FREECAD ASSEMBLY — COMPONENT RECIPES ("assambly-control-assembly")

This assembly document has 2 components, labeled P0..P1 below (a component is one placed body or linked part). 2 of them carry a construction recipe — the FreeCAD feature program that regenerates the part from scratch, quoted from this document or its linked companion documents; the rest are supplied as boundary geometry only. No exploded tour is included for this assembly.
COMPONENT P0 — recipe-attached ("SideBody", a linked part whose construction recipe lives in a companion FreeCAD document of the same project; that document's serialized recipe follows).
Construction recipe (the companion document, serialized — sketch geometry with constraints, then the solid features built on it; lengths are millimeters unless a unit is written):

FCSTD DOCUMENT  (FreeCAD 1.0RUnknown)
Label: assambly-control-varset
License: All rights reserved
LicenseURL: https://en.wikipedia.org/wiki/All_rights_reserved
objects: Sketcher::SketchObject×3, PartDesign::Pad×2, PartDesign::Body×2, App::VarSet×1
note: 14 computed .brp shape members not serialized (recipe doc carries the construction recipe); baked Part::Feature solids carry a one-line shape summary decoded from their .brp

FEATURE [Sketcher::SketchObject] Sketch  label="SkeletonSketch"
  ArcFitTolerance = 1e-06
  FullyConstrained = true
  MakeInternals = false
  Placement = pos=(0,0,0) rot=(1,0,0;1.5708rad)
  expr: Constraints[20] = VarSet.Shelf3Haight
  expr: Constraints[21] = VarSet.Shelf2Height
  expr: Constraints[22] = VarSet.Shelf1Height
  expr: Constraints[7] = VarSet.CabWidth
  expr: Constraints[8] = VarSet.CabHeight
  sketch-geometry (7):
    g0: LineSegment StartX=-500 StartY=0 StartZ=0 EndX=500 EndY=0 EndZ=0
    g1: LineSegment StartX=500 StartY=0 StartZ=0 EndX=500 EndY=2500 EndZ=0
    g2: LineSegment StartX=500 StartY=2500 StartZ=0 EndX=-500 EndY=2500 EndZ=0
    g3: LineSegment StartX=-500 StartY=2500 StartZ=0 EndX=-500 EndY=0 EndZ=0
    g4: LineSegment StartX=-500 StartY=500 StartZ=0 EndX=500 EndY=500 EndZ=0
    g5: LineSegment StartX=-500 StartY=1000 StartZ=0 EndX=500 EndY=1000 EndZ=0
    g6: LineSegment StartX=-500 StartY=1500 StartZ=0 EndX=500 EndY=1500 EndZ=0
  constraints (23):
    c: Coincident(g0,g1)
    c: Coincident(g1,g2)
    c: Coincident(g2,g3)
    c: Coincident(g3,g0)
    c: Horizontal(g2)
    c: Vertical(g1)
    c: Vertical(g3)
    c: Distance(g1,g3) = 1000
    c: Distance(g0,g2) = 2500
    c: PointOnObject(g0,g-1)
    c: Symmetric(g0,g0,g-2)
    c: PointOnObject(g4,g3)
    c: PointOnObject(g4,g1)
    c: Horizontal(g4)
    c: PointOnObject(g5,g3)
    c: PointOnObject(g5,g1)
    c: Horizontal(g5)
    c: PointOnObject(g6,g3)
    c: PointOnObject(g6,g1)
    c: Horizontal(g6)
    c: DistanceY(g-1,g4) = 500
    c: DistanceY(g-1,g5) = 1000
    c: DistanceY(g-1,g6) = 1500
FEATURE [App::VarSet] VarSet
  CabHeight = 2580
  CabWidth = 1000
  Shelf1Height = 1500
  Shelf2Height = 1000
  Shelf3Haight = 500
FEATURE [Sketcher::SketchObject] Sketch001
  ArcFitTolerance = 1e-06
  AttachmentSupport = -> [YZ_Plane]
  FullyConstrained = true
  MakeInternals = false
  MapMode = 5
  Placement = pos=(0,0,0) rot=(0.57735,0.57735,0.57735;2.0944rad)
  expr: Constraints[8] = VarSet.CabWidth
  expr: Constraints[9] = VarSet.CabHeight
  sketch-geometry (4):
    g0: LineSegment StartX=-500 StartY=0 StartZ=0 EndX=500 EndY=0 EndZ=0
    g1: LineSegment StartX=500 StartY=0 StartZ=0 EndX=500 EndY=2500 EndZ=0
    g2: LineSegment StartX=500 StartY=2500 StartZ=0 EndX=-500 EndY=2500 EndZ=0
    g3: LineSegment StartX=-500 StartY=2500 StartZ=0 EndX=-500 EndY=0 EndZ=0
  constraints (11):
    c: Coincident(g0,g1)
    c: Coincident(g1,g2)
    c: Coincident(g2,g3)
    c: Coincident(g3,g0)
    c: Horizontal(g0)
    c: Horizontal(g2)
    c: Vertical(g1)
    c: Vertical(g3)
    c: Distance(g0,g0) = 1000
    c: DistanceY(g1,g1) = 2500
    c: Symmetric(g0,g0,g-1)
FEATURE [PartDesign::Pad] Pad
  Direction = (1,0,0)
  Length = 30
  Length2 = 10
  Placement = pos=(0,0,0) rot=(1,1,1;2.0944rad)
  Profile = -> Sketch001
  ReferenceAxis = -> Sketch001 [N_Axis]
  Refine = true
  Suppressed = false
  Type = 0
FEATURE [PartDesign::Body] Body  label="SideBody"
  AllowCompound = false
  Group = -> [Sketch001,Pad]
  Origin = -> Origin
  Tip = -> Pad
FEATURE [Sketcher::SketchObject] Sketch002
  ArcFitTolerance = 1e-06
  AttachmentSupport = -> [XY_Plane001]
  FullyConstrained = true
  MakeInternals = false
  MapMode = 5
  expr: Constraints[10] = VarSet.CabWidth
  sketch-geometry (5):
    g0: LineSegment StartX=500 StartY=-500 StartZ=0 EndX=500 EndY=500 EndZ=0
    g1: LineSegment StartX=500 StartY=500 StartZ=0 EndX=-500 EndY=500 EndZ=0
    g2: LineSegment StartX=-500 StartY=500 StartZ=0 EndX=-500 EndY=-500 EndZ=0
    g3: LineSegment StartX=-500 StartY=-500 StartZ=0 EndX=500 EndY=-500 EndZ=0
    g4: GeomPoint [constr] X=0 Y=0 Z=0
  constraints (12):
    c: Coincident(g0,g1)
    c: Coincident(g1,g2)
    c: Coincident(g2,g3)
    c: Coincident(g3,g0)
    c: Vertical(g0)
    c: Vertical(g2)
    c: Horizontal(g1)
    c: Horizontal(g3)
    c: Symmetric(g2,g0,g4)
    c: Coincident(g4,g-1)
    c: DistanceY(g2,g2) = 1000
    c: Equal(g2,g1)
FEATURE [PartDesign::Pad] Pad001
  Direction = (0,0,1)
  Length = 30
  Length2 = 10
  Profile = -> Sketch002
  ReferenceAxis = -> Sketch002 [N_Axis]
  Refine = true
  Suppressed = false
  Type = 0
FEATURE [PartDesign::Body] Body001  label="ShelfBody"
  AllowCompound = false
  Group = -> [Sketch002,Pad001]
  Origin = -> Origin001
  Tip = -> Pad001
COMPONENT P1 — same part as P0; its construction recipe is shown at P0.
PROVENANCE & LICENSES
A FreeCAD (.FCStd) document from a public repository crawl; recipes are the document's own serialized feature recipes (and, for linked parts, companion documents' recipes).
License: as declared in the source repository (recorded in the dataset sidecar).
